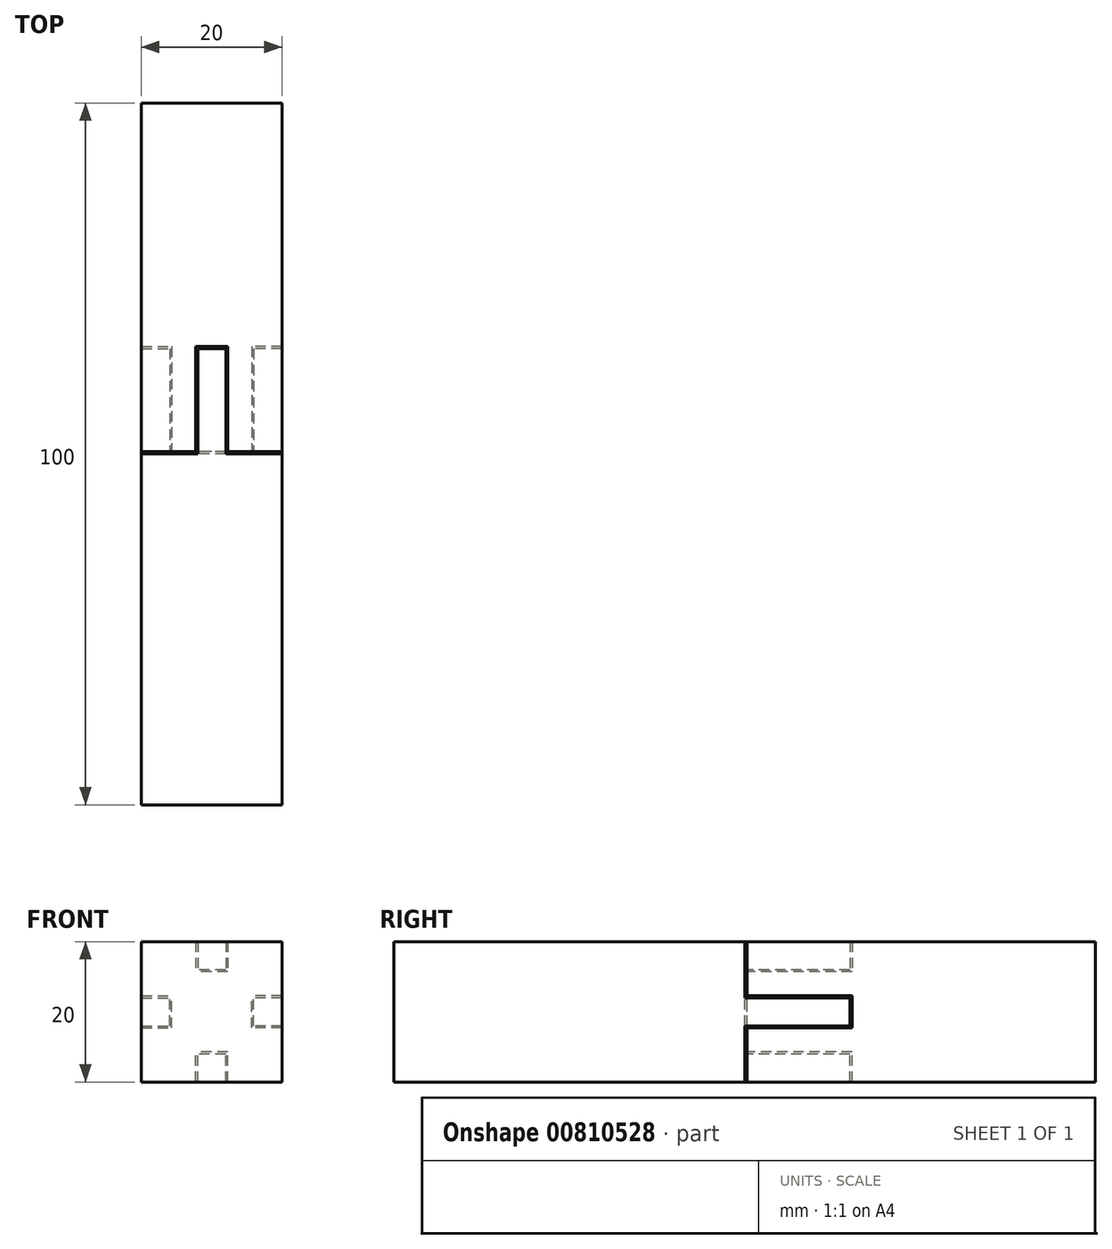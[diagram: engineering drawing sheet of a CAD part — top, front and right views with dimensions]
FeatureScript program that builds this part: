
annotation { "Feature Type Name" : "Feature", "Feature Type Description" : "" }
export const myFeature = defineFeature(function(context is Context, id is Id, definition is map)
    precondition{}
    {
        {
            var Q0;
            Q0=qCreatedBy(makeId("Front.planeOp"),FACE);
            var sketch = newSketch(context, id + "F0", { "sketchPlane" : qUnion([Q0])});
            skLineSegment(sketch, "E0.bottom", {"start": v(10, 10) * mm, "end": v(-10, 10) * mm});
            skLineSegment(sketch, "E0.top", {"start": v(10, -10) * mm, "end": v(-10, -10) * mm});
            skLineSegment(sketch, "E0.left", {"start": v(10, 10) * mm, "end": v(10, -10) * mm});
            skLineSegment(sketch, "E0.right", {"start": v(-10, 10) * mm, "end": v(-10, -10) * mm});
            skPoint(sketch, "E0.middle", {"position": v(0, 0) * mm});
            skSolve(sketch);
        }
        {
            var Q0;
            Q0=makeQuery(id+"F0.imprint","IMPRINT",FACE,{"disambiguationData":[TD([[makeQuery(id+"F0.imprint","IMPRINT",EDGE,{"derivedFrom":sQuery(id+"F0.wireOp",EDGE,"E0.bottom")}),1.0]])]});
            extrude(context, id + "F1", {"entities" : qUnion([Q0]), "depth" : 50 * mm, "offsetDistance" : 25 * mm});
        }
        {
            var Q0;
            Q0=makeQuery(id+"F1.opExtrude","CAP_FACE",FACE,{"disambiguationData":[OSD([sQuery(id+"F0.wireOp",EDGE,"E0.bottom"),sQuery(id+"F0.wireOp",EDGE,"E0.top"),sQuery(id+"F0.wireOp",EDGE,"E0.left"),sQuery(id+"F0.wireOp",EDGE,"E0.right")])],"isStart":true});
            var sketch = newSketch(context, id + "F2", { "sketchPlane" : qUnion([Q0])});
            skLineSegment(sketch, "E1.bottom", {"start": v(-2, 10) * mm, "end": v(2, 10) * mm});
            skLineSegment(sketch, "E1.top", {"start": v(-2, 6) * mm, "end": v(2, 6) * mm});
            skLineSegment(sketch, "E1.left", {"start": v(-2, 10) * mm, "end": v(-2, 6) * mm});
            skLineSegment(sketch, "E1.right", {"start": v(2, 10) * mm, "end": v(2, 6) * mm});
            skLineSegment(sketch, "E2.bottom", {"start": v(-2, -10) * mm, "end": v(2, -10) * mm});
            skLineSegment(sketch, "E2.top", {"start": v(-2, -6) * mm, "end": v(2, -6) * mm});
            skLineSegment(sketch, "E2.left", {"start": v(-2, -10) * mm, "end": v(-2, -6) * mm});
            skLineSegment(sketch, "E2.right", {"start": v(2, -10) * mm, "end": v(2, -6) * mm});
            skPoint(sketch, "E3", {"position": v(0, 10) * mm});
            skPoint(sketch, "E4", {"position": v(0, -10) * mm});
            skLineSegment(sketch, "E5.bottom", {"start": v(-10, -2) * mm, "end": v(-6, -2) * mm});
            skLineSegment(sketch, "E5.top", {"start": v(-10, 2) * mm, "end": v(-6, 2) * mm});
            skLineSegment(sketch, "E5.left", {"start": v(-10, -2) * mm, "end": v(-10, 2) * mm});
            skLineSegment(sketch, "E5.right", {"start": v(-6, -2) * mm, "end": v(-6, 2) * mm});
            skLineSegment(sketch, "E6.bottom", {"start": v(10, -2) * mm, "end": v(6, -2) * mm});
            skLineSegment(sketch, "E6.top", {"start": v(10, 2) * mm, "end": v(6, 2) * mm});
            skLineSegment(sketch, "E6.left", {"start": v(10, -2) * mm, "end": v(10, 2) * mm});
            skLineSegment(sketch, "E6.right", {"start": v(6, -2) * mm, "end": v(6, 2) * mm});
            skPoint(sketch, "E7", {"position": v(-10, 0) * mm});
            skPoint(sketch, "E8", {"position": v(10, 0) * mm});
            skSolve(sketch);
        }
        {
            var Q0;
            Q0 = qSketchRegion(id + "F2", true);
            extrude(context, id + "F3", {"entities" : qUnion([Q0]), "operationType" : NewBodyOperationType.ADD, "depth" : 15 * mm, "offsetDistance" : 25 * mm});
        }
        {
            var Q0;
            Q0=qCreatedBy(makeId("Front.planeOp"),FACE);
            var sketch = newSketch(context, id + "F4", { "sketchPlane" : qUnion([Q0])});
            skPoint(sketch, "E9.middle", {"position": v(0, 0) * mm});
            skLineSegment(sketch, "E10.0", {"start": v(10, 10) * mm, "end": v(2, 10) * mm, "construction": true});
            skLineSegment(sketch, "E11.0", {"start": v(-10, -2) * mm, "end": v(-10, -10) * mm, "construction": true});
            skLineSegment(sketch, "E12.bottom", {"start": v(10, 10) * mm, "end": v(-10, 10) * mm});
            skLineSegment(sketch, "E12.top", {"start": v(10, -10) * mm, "end": v(-10, -10) * mm});
            skLineSegment(sketch, "E12.left", {"start": v(10, 10) * mm, "end": v(10, -10) * mm});
            skLineSegment(sketch, "E12.right", {"start": v(-10, 10) * mm, "end": v(-10, -10) * mm});
            skSolve(sketch);
        }
        {
            var Q0;
            Q0 = qSketchRegion(id + "F4", true);
            extrude(context, id + "F5", {"entities" : qUnion([Q0]), "oppositeDirection" : true, "depth" : 50 * mm, "offsetDistance" : 25 * mm});
        }
        {
            var Q0;
            Q0=makeQuery(id+"F1.opExtrude","SWEPT_BODY",BODY,{"disambiguationData":[OSD([sQuery(id+"F0.wireOp",EDGE,"E0.bottom"),sQuery(id+"F0.wireOp",EDGE,"E0.top"),sQuery(id+"F0.wireOp",EDGE,"E0.left"),sQuery(id+"F0.wireOp",EDGE,"E0.right")])]});
            var Q1;
            Q1=makeQuery(id+"F5.opExtrude","SWEPT_BODY",BODY,{"disambiguationData":[OSD([sQuery(id+"F4.wireOp",EDGE,"E12.bottom"),sQuery(id+"F4.wireOp",EDGE,"E12.top"),sQuery(id+"F4.wireOp",EDGE,"E12.left"),sQuery(id+"F4.wireOp",EDGE,"E12.right")])]});
            booleanBodies(context, id + "F6", {"operationType" : BooleanOperationType.SUBTRACTION, "tools" : qUnion([Q0]), "targets" : qUnion([Q1]), "offset" : true, "offsetAll" : true, "offsetDistance" : 0.3 * mm, "keepTools" : true});
        }
    });
